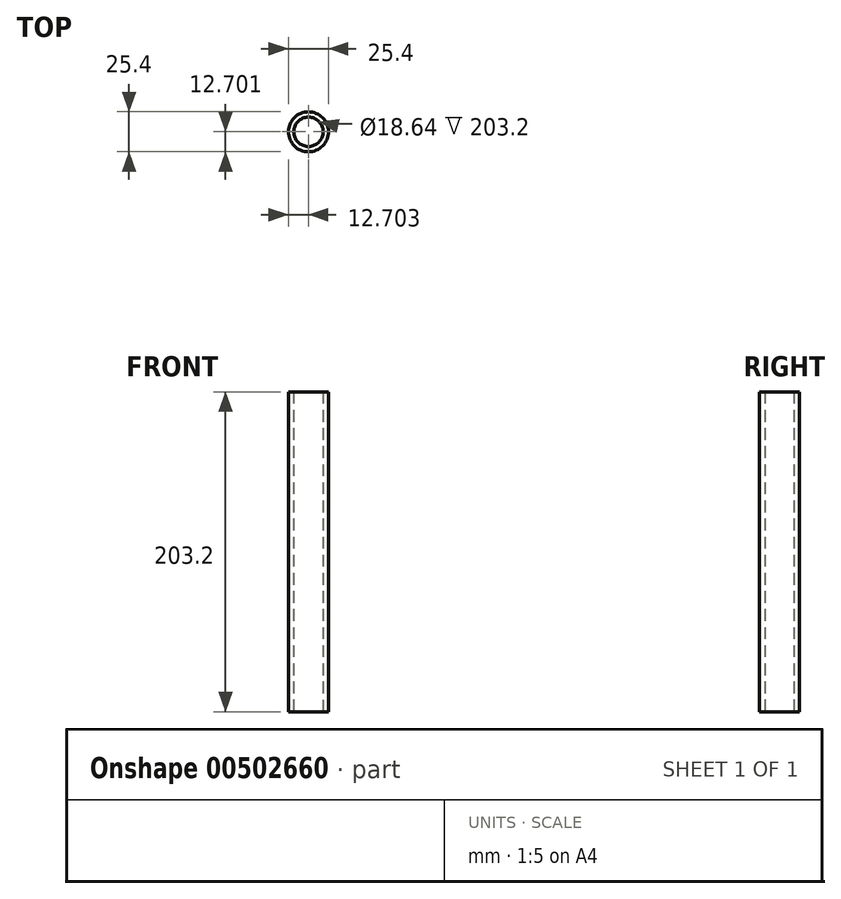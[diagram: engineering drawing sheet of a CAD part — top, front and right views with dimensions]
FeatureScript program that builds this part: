
annotation { "Feature Type Name" : "Feature", "Feature Type Description" : "" }
export const myFeature = defineFeature(function(context is Context, id is Id, definition is map)
    precondition{}
    {
        {
            var Q0;
            Q0=qCreatedBy(makeId("Top.planeOp"),FACE);
            var sketch = newSketch(context, id + "F0", { "sketchPlane" : qUnion([Q0])});
            skCircle(sketch, "E0", {"center": v(47.58, -48.34) * mm, "radius": 12.7 * mm});
            skCircle(sketch, "E1", {"center": v(47.58, -48.34) * mm, "radius": 9.32 * mm});
            skCircle(sketch, "E2", {"center": v(-58.04, -192.54) * mm, "radius": 58.48 * mm});
            skSolve(sketch);
        }
        {
            var Q0;
            Q0=makeQuery(id+"F0.imprint","IMPRINT",FACE,{"disambiguationData":[TD([[makeQuery(id+"F0.imprint","IMPRINT",EDGE,{"derivedFrom":sQuery(id+"F0.wireOp",EDGE,"E0")}),1.0]])]});
            extrude(context, id + "F1", {"entities" : qUnion([Q0]), "depth" : 203.2 * mm});
        }
    });
